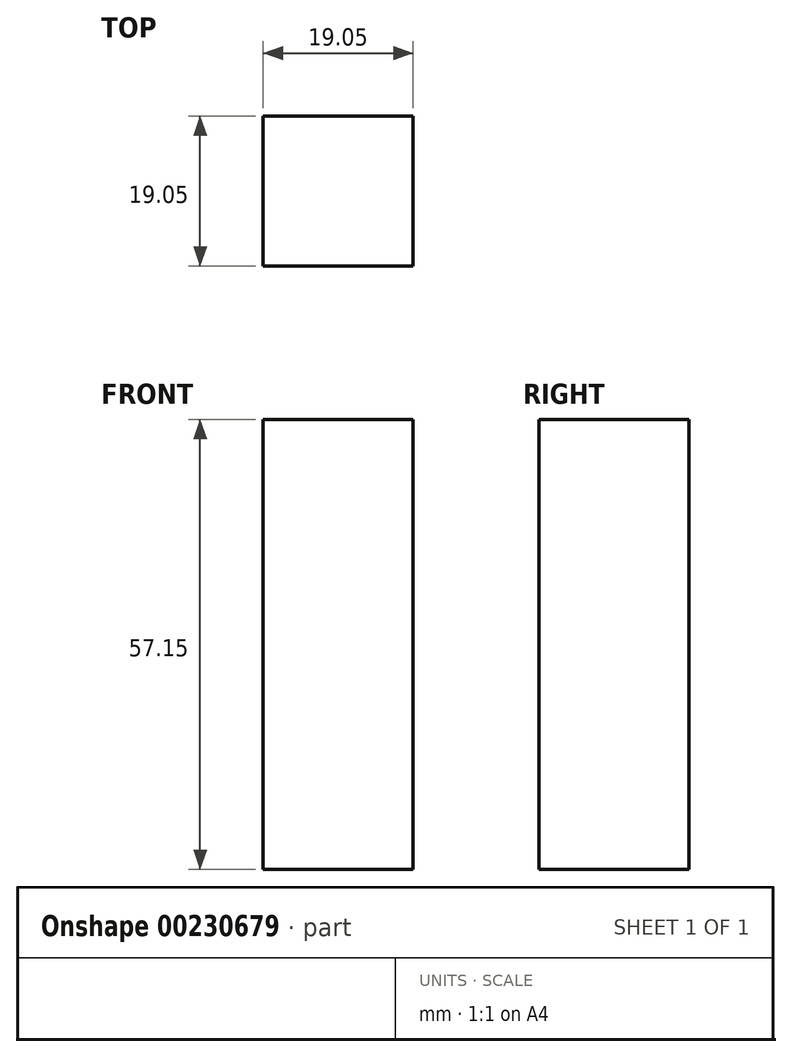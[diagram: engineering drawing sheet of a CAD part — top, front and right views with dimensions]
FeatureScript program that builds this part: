
annotation { "Feature Type Name" : "Feature", "Feature Type Description" : "" }
export const myFeature = defineFeature(function(context is Context, id is Id, definition is map)
    precondition{}
    {
        {
            var Q0;
            Q0=qCreatedBy(makeId("Front.planeOp"),FACE);
            var sketch = newSketch(context, id + "F0", { "sketchPlane" : qUnion([Q0])});
            skLineSegment(sketch, "E0.bottom", {"start": v(-46.71, 48.8) * mm, "end": v(-27.66, 48.8) * mm});
            skLineSegment(sketch, "E0.top", {"start": v(-46.71, -8.34) * mm, "end": v(-27.66, -8.34) * mm});
            skLineSegment(sketch, "E0.left", {"start": v(-46.71, 48.8) * mm, "end": v(-46.71, -8.34) * mm});
            skLineSegment(sketch, "E0.right", {"start": v(-27.66, 48.8) * mm, "end": v(-27.66, -8.34) * mm});
            skSolve(sketch);
        }
        {
            var Q0;
            Q0 = qSketchRegion(id + "F0", true);
            extrude(context, id + "F1", {"entities" : qUnion([Q0]), "depth" : 19.05 * mm});
        }
    });
